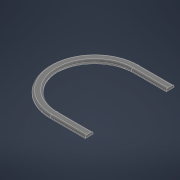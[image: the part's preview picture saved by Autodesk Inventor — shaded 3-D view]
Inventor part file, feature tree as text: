
AUTODESK INVENTOR PART (.ipt)
format: ipt  version: 2022 (Build 260153000, 153)  size: 322,560 bytes
history: native  units: mm
features: extrude x2, sketch x2, fillet x1
ambient origin geometry x8: Origin, YZ Plane, XZ Plane, XY Plane, X Axis, Y Axis, Z Axis, Center Point
bodies: Solid1 (feature_tree)
feature tree (5):
  extrude  "Extrusion1"  Depth=3.0mm TaperAngle=0.0deg
  extrude  "Extrusion2"  Depth=2.0mm
  fillet  "Fillet1"  [1 undecoded]
  sketch  "Sketch1"  dims[d7=3.0mm d8=3.0mm d9=0.0mm]
  sketch  "Sketch2"  dims[d11=3.0mm d12=0.0mm d13=2.0mm]
note: 1 required parameter value undecoded (feature->parameter linkage not recoverable at this tier; creation-order binding heuristic only, values carry confidence <= 0.55)
